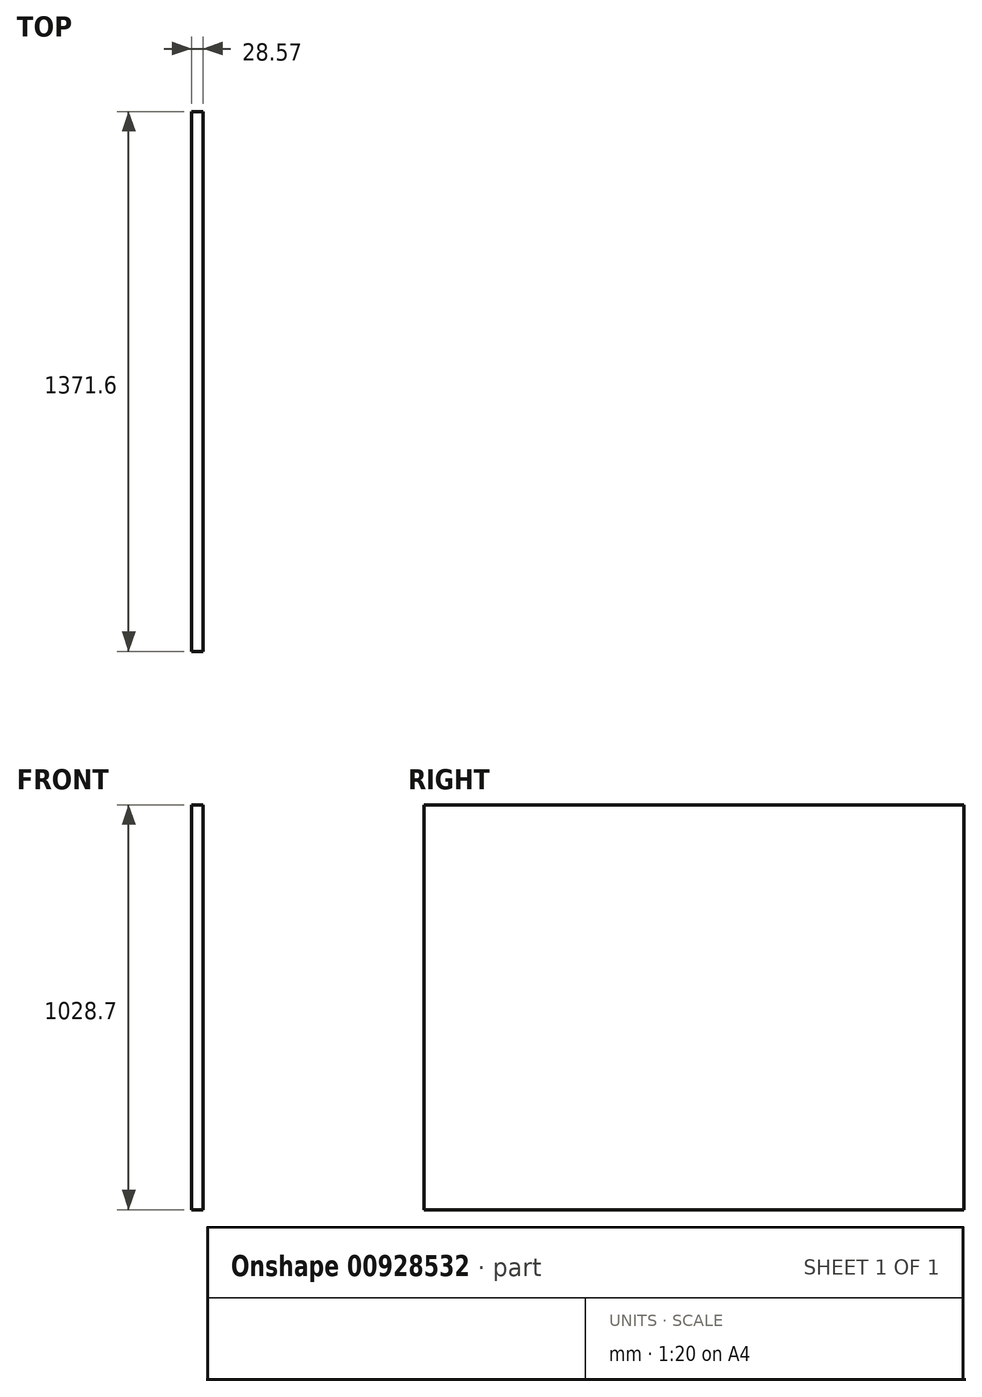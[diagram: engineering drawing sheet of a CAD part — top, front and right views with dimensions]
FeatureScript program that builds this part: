
annotation { "Feature Type Name" : "Feature", "Feature Type Description" : "" }
export const myFeature = defineFeature(function(context is Context, id is Id, definition is map)
    precondition{}
    {
        {
            var Q0;
            Q0=qCreatedBy(makeId("Right.planeOp"),FACE);
            var sketch = newSketch(context, id + "F0", { "sketchPlane" : qUnion([Q0])});
            skLineSegment(sketch, "E0.bottom", {"start": v(685.8, 514.35) * mm, "end": v(-685.8, 514.35) * mm});
            skLineSegment(sketch, "E0.top", {"start": v(685.8, -514.35) * mm, "end": v(-685.8, -514.35) * mm});
            skLineSegment(sketch, "E0.left", {"start": v(685.8, 514.35) * mm, "end": v(685.8, -514.35) * mm});
            skLineSegment(sketch, "E0.right", {"start": v(-685.8, 514.35) * mm, "end": v(-685.8, -514.35) * mm});
            skPoint(sketch, "E0.middle", {"position": v(0, 0) * mm});
            skSolve(sketch);
        }
        {
            var Q0;
            Q0=makeQuery(id+"F0.imprint","IMPRINT",FACE,{"disambiguationData":[TD([[makeQuery(id+"F0.imprint","IMPRINT",EDGE,{"derivedFrom":sQuery(id+"F0.wireOp",EDGE,"E0.bottom")}),1.0]])]});
            extrude(context, id + "F1", {"entities" : qUnion([Q0]), "depth" : 28.57 * mm, "offsetDistance" : 25.4 * mm});
        }
    });
